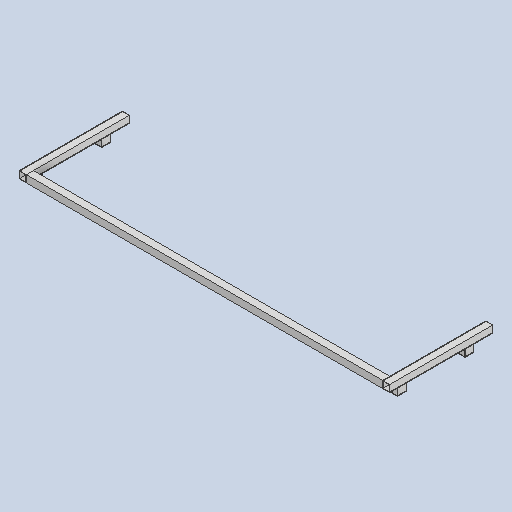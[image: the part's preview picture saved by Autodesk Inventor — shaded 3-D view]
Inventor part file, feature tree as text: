
AUTODESK INVENTOR PART (.ipt)
format: ipt  version: 2025 (Build 290162000, 162)  size: 160,768 bytes
history: native  units: mm
features: extrude x3, shell x2, projected_geometry x2, sketch x1
ambient origin geometry x8: Origin, YZ Plane, XZ Plane, XY Plane, X Axis, Y Axis, Z Axis, Center Point
bodies: Solid1 (feature_tree), Solid2 (feature_tree), Solid4 (feature_tree)
feature tree (8):
  extrude  "Extrusion1"  Depth=725.0mm
  extrude  "Extrusion2"  Depth=50.0mm
  shell  "Shell1"  Thickness=50.0mm
  extrude  "Extrusion4"  Depth=50.0mm TaperAngle=0.0deg
  shell  "Shell3"  Thickness=250.0mm
  projected_geometry  "Projected Loop1"
  projected_geometry  "Projected Loop2"
  sketch  "Sketch Rectangular Pattern1"  dims[d0=2608.0mm d1=725.0mm d2=50.0mm d3=50.0mm d4=0.0mm d5=50.0mm d6=0.0mm d7=250.0mm d8=3.0mm d28=50.0mm d29=60.0mm d30=55.0mm d31=20.0mm d33=2558.0mm d34=20.0mm d36=475.0mm d39=50.0mm d40=0.0mm d41=3.0mm]
